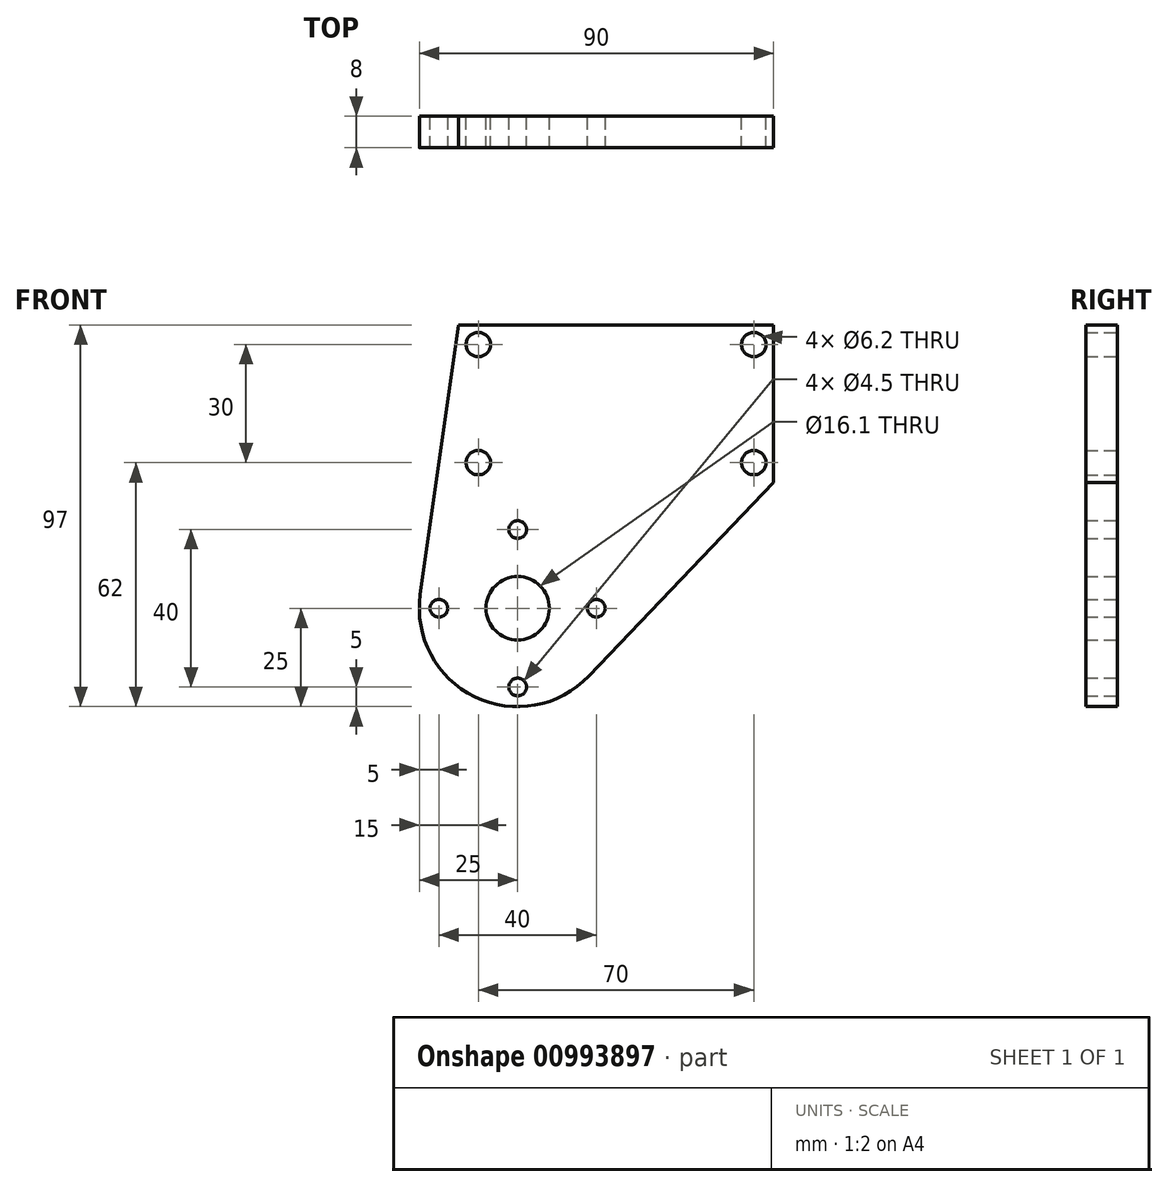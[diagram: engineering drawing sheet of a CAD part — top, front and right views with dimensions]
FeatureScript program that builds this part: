
annotation { "Feature Type Name" : "Feature", "Feature Type Description" : "" }
export const myFeature = defineFeature(function(context is Context, id is Id, definition is map)
    precondition{}
    {
        {
            var Q0;
            Q0=qCreatedBy(makeId("Front.planeOp"),FACE);
            var sketch = newSketch(context, id + "F0", { "sketchPlane" : qUnion([Q0])});
            skPoint(sketch, "E0.middle", {"position": v(0, 0) * mm});
            skLineSegment(sketch, "E1.top", {"start": v(-15, 72) * mm, "end": v(65, 72) * mm});
            skLineSegment(sketch, "E1.right", {"start": v(65, 32) * mm, "end": v(65, 72) * mm});
            skPoint(sketch, "E1.middle", {"position": v(25, 52) * mm});
            skCircle(sketch, "E2", {"center": v(0, 0) * mm, "radius": 8.05 * mm});
            skArc(sketch, "E3", {"start": v(-24.75, 3.52) * mm, "mid": v(-10.9, -22.5) * mm, "end": v(18.1, -17.24) * mm});
            skCircle(sketch, "E4", {"center": v(-10, 67) * mm, "radius": 3.1 * mm});
            skCircle(sketch, "E5", {"center": v(60, 67) * mm, "radius": 3.1 * mm});
            skCircle(sketch, "E6", {"center": v(60, 37) * mm, "radius": 3.1 * mm});
            skCircle(sketch, "E7", {"center": v(-10, 37) * mm, "radius": 3.1 * mm});
            skLineSegment(sketch, "E8", {"start": v(-15, 72) * mm, "end": v(-24.75, 3.52) * mm});
            skLineSegment(sketch, "E9", {"start": v(65, 32) * mm, "end": v(18.1, -17.24) * mm});
            skCircle(sketch, "E10", {"center": v(0, 0) * mm, "radius": 20 * mm, "construction": true});
            skCircle(sketch, "E11", {"center": v(0, 20) * mm, "radius": 2.25 * mm});
            skCircle(sketch, "E12", {"center": v(-20, 0) * mm, "radius": 2.25 * mm});
            skCircle(sketch, "E13", {"center": v(20, 0) * mm, "radius": 2.25 * mm});
            skCircle(sketch, "E14", {"center": v(0, -20) * mm, "radius": 2.25 * mm});
            skSolve(sketch);
        }
        {
            var Q0;
            Q0=qSketchRegion(id+"F0",true);
            extrude(context, id + "F1", {"entities" : qUnion([Q0]), "depth" : 8 * mm, "offsetDistance" : 25 * mm});
        }
    });
